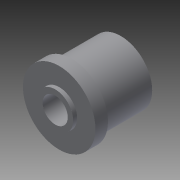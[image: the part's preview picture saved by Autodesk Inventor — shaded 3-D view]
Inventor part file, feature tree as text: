
AUTODESK INVENTOR PART (.ipt)
format: ipt  version: 2014 (Build 180170000, 170)  size: 110,592 bytes
history: native  units: mm
features: extrude x4, sketch x4
ambient origin geometry x8: Origin, YZ Plane, XZ Plane, XY Plane, X Axis, Y Axis, Z Axis, Center Point
bodies: Solid1 (feature_tree)
feature tree (8):
  extrude  "Extrusion1"  Depth=4.4mm
  extrude  "Extrusion2"  Depth=0.7mm
  extrude  "Extrusion3"  Depth=2.2mm
  extrude  "Extrusion4"  Depth=0.7mm TaperAngle=0.0deg
  sketch  "Sketch1"  dims[d0=6.3mm d1=4.4mm]
  sketch  "Sketch2"  dims[d2=0.7mm d3=0.0mm d4=12.7mm]
  sketch  "Sketch3"  dims[d5=2.2mm d6=0.0mm d7=11.0mm]
  sketch  "Sketch4"  dims[d8=8.6mm d9=0.0mm d10=0.7mm d11=0.0mm]
